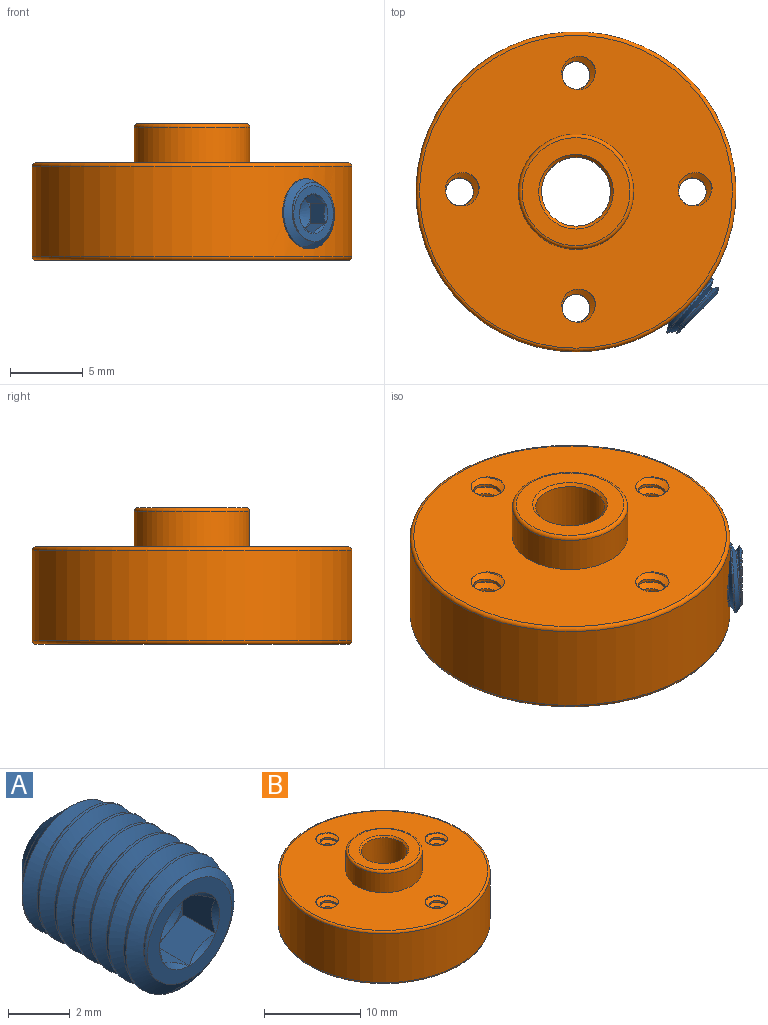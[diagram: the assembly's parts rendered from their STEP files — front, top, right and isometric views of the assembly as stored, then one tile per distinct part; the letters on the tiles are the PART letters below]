
ASSEMBLY  parts=2 mates=1
PART A: 27 faces, bbox 4.8x6.8x4.8 mm
  f0: plane 1.03x0.6mm, normal (0,-1,0), area 0.1mm2, adj f20,f21,f26
  f1: plane 1.19x0.34mm, normal (0,-1,0), area 0.1mm2, adj f20,f25,f26
  f2: plane 1.03x0.6mm, normal (0,-1,0), area 0.1mm2, adj f24,f25,f26
  f3: plane 1.03x0.6mm, normal (0,-1,0), area 0.1mm2, adj f23,f24,f26
  f4: plane 1.19x0.34mm, normal (0,-1,0), area 0.1mm2, adj f22,f23,f26
  f5: plane 3.86x3.84mm, normal (0,-1,0), area 5.7mm2, adj f6,f10,f11,f12,f13,f14,f15,f16
  f6: cone r=2.41mm half-angle=55deg, axis (0,1,0), area 3.7mm2, adj f5,f7,f10,f12
  f7: cylinder r=2.41mm len=4.92mm, axis (0,-1,0), area 9.3mm2, adj f6,f8,f10,f12
  f8: cone r=1.32mm half-angle=45deg, axis (0,-1,0), area 13mm2, adj f7,f9,f10,f11,f12
  f9: cone r=0mm half-angle=59deg, axis (0,1,0), area 6.4mm2, adj f8
  f10: bspline ~6.25x4.83mm, area 54.3mm2, adj f5,f6,f7,f8,f11
  f11: cylinder r=1.9mm len=5.77mm, axis (0,-1,0), area 8.6mm2, adj f5,f8,f10,f12
  f12: bspline ~6.25x4.83mm, area 54.2mm2, adj f5,f6,f7,f8,f11
  f13: cone r=1.37mm half-angle=45deg, axis (0,-1,0), area 0.2mm2, adj f5,f20
  f14: cone r=1.37mm half-angle=45deg, axis (0,-1,0), area 0.2mm2, adj f5,f21
  f15: cone r=1.37mm half-angle=45deg, axis (0,-1,0), area 0.2mm2, adj f5,f22
  f16: cone r=1.37mm half-angle=45deg, axis (0,-1,0), area 0.2mm2, adj f5,f23
  f17: cone r=1.37mm half-angle=45deg, axis (0,-1,0), area 0.2mm2, adj f5,f24
  f18: cone r=1.37mm half-angle=45deg, axis (0,-1,0), area 0.2mm2, adj f5,f25
  f19: plane 1.03x0.6mm, normal (0,-1,0), area 0.1mm2, adj f21,f22,f26
  f20: plane 1.49x1.19mm, normal (0.5,0,-0.87), area 1.9mm2, adj f0,f1,f13,f21,f25
  f21: plane 1.49x1.38mm, normal (1,0,0), area 1.9mm2, adj f0,f14,f19,f20,f22
  f22: plane 1.49x1.19mm, normal (0.5,0,0.87), area 1.9mm2, adj f4,f15,f19,f21,f23
  f23: plane 1.49x1.19mm, normal (-0.5,0,0.87), area 1.9mm2, adj f3,f4,f16,f22,f24
  f24: plane 1.49x1.38mm, normal (-1,0,0), area 1.9mm2, adj f2,f3,f17,f23,f25
  f25: plane 1.49x1.19mm, normal (-0.5,0,-0.87), area 1.9mm2, adj f1,f2,f18,f20,f24
  f26: cone r=1.19mm half-angle=60deg, axis (0,-1,0), area 5.1mm2, adj f0,f1,f2,f3,f4,f19
PART B: 28 faces, bbox 24x24x10 mm
  f0: plane 21.71x21.71mm, normal (0,0,1), area 297mm2, adj f3,f9,f12,f13,f14,f15,f16,f17
  f1: plane 21.71x21.71mm, normal (0,0,-1), area 325.6mm2, adj f4,f6,f12,f13,f14,f15,f16,f17
  f2: torus R=3.71mm, axis (0,0,1), area 9.6mm2, adj f9,f11
  f3: torus R=10.75mm, axis (0,0,1), area 26.9mm2, adj f0,f10
  f4: torus R=10.75mm, axis (0,0,1), area 26.9mm2, adj f1,f10
  f5: cone r=2.36mm half-angle=45deg, axis (0,0,1), area 4.4mm2, adj f8,f11
  f6: cone r=2.56mm half-angle=45deg, axis (0,0,-1), area 4.4mm2, adj f1,f8
  f7: cylinder r=2mm len=9.58mm, axis (-0.71,-0.71,0), area 112.5mm2, adj f8,f10
  f8: cylinder r=2.36mm len=9mm, axis (0,0,1), area 119.7mm2, adj f5,f6,f7
  f9: cylinder r=3.96mm len=7.93mm, axis (0,0,-1), area 61mm2, adj f0,f2
  f10: cylinder r=11mm len=22mm, axis (0,0,1), area 415.9mm2, adj f3,f4,f7
  f11: plane 7.43x7.43mm, normal (0,0,1), area 22.6mm2, adj f2,f5
  f12: bspline ~7.26x3.19mm, area 30.8mm2, adj f0,f1,f14,f15
  f13: bspline ~7.39x3.19mm, area 30.8mm2, adj f0,f1,f14,f15
  f14: bspline ~6.98x3.28mm, area 8.5mm2, adj f0,f1,f12,f13
  f15: cylinder r=0.95mm len=6.7mm, axis (0,0,-1), area 12.9mm2, adj f0,f1,f12,f13
  f16: bspline ~7.26x3.19mm, area 30.8mm2, adj f0,f1,f18,f19
  f17: bspline ~7.39x3.19mm, area 30.8mm2, adj f0,f1,f18,f19
  f18: bspline ~6.98x3.28mm, area 8.5mm2, adj f0,f1,f16,f17
  f19: cylinder r=0.95mm len=6.7mm, axis (0,0,-1), area 12.9mm2, adj f0,f1,f16,f17
  f20: bspline ~7.26x3.19mm, area 30.8mm2, adj f0,f1,f22,f23
  f21: bspline ~7.39x3.19mm, area 30.8mm2, adj f0,f1,f22,f23
  f22: bspline ~6.98x3.28mm, area 8.5mm2, adj f0,f1,f20,f21
  f23: cylinder r=0.95mm len=6.7mm, axis (0,0,-1), area 12.9mm2, adj f0,f1,f20,f21
  f24: bspline ~7.26x3.19mm, area 30.8mm2, adj f0,f1,f26,f27
  f25: bspline ~7.39x3.19mm, area 30.8mm2, adj f0,f1,f26,f27
  f26: bspline ~6.98x3.28mm, area 8.5mm2, adj f0,f1,f24,f25
  f27: cylinder r=0.95mm len=6.7mm, axis (0,0,-1), area 12.9mm2, adj f0,f1,f24,f25
PLACE A rot(axis=(0,0,1),45deg) t=(6.39,-6.41,3.2)mm
PLACE B rot(axis=(0,0,-1),90deg) t=(0,-0.01,6.7)mm
MATE fastened A.f11 <-> B.f7  axis (0.71,-0.71,0) through (8.35,-8.37,3.2)mm
